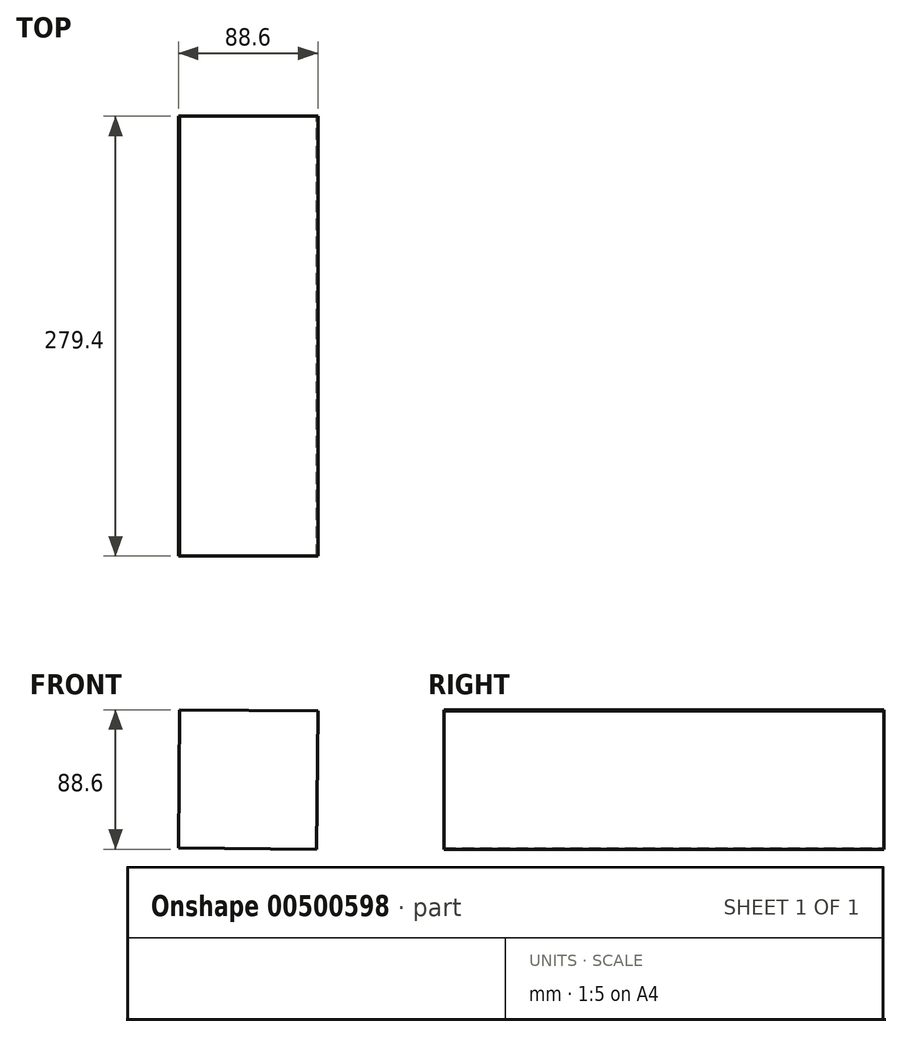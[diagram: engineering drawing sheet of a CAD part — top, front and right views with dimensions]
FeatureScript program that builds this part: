
annotation { "Feature Type Name" : "Feature", "Feature Type Description" : "" }
export const myFeature = defineFeature(function(context is Context, id is Id, definition is map)
    precondition{}
    {
        {
            var Q0;
            Q0=qCreatedBy(makeId("Front.planeOp"),FACE);
            var sketch = newSketch(context, id + "F0", { "sketchPlane" : qUnion([Q0])});
            skCircle(sketch, "E0.cCircle", {"center": v(0, 3.06) * mm, "radius": 62.04 * mm, "construction": true});
            skLineSegment(sketch, "E0.0", {"start": v(44.3, 46.5) * mm, "end": v(43.43, -41.24) * mm});
            skLineSegment(sketch, "E0.1", {"start": v(43.43, -41.24) * mm, "end": v(-44.3, -40.37) * mm});
            skLineSegment(sketch, "E0.2", {"start": v(-44.3, -40.37) * mm, "end": v(-43.43, 47.36) * mm});
            skLineSegment(sketch, "E0.3", {"start": v(-43.43, 47.36) * mm, "end": v(44.3, 46.5) * mm});
            skSolve(sketch);
        }
        {
            var Q0;
            Q0 = qSketchRegion(id + "F0", true);
            extrude(context, id + "F1", {"entities" : qUnion([Q0]), "depth" : 279.4 * mm});
        }
    });
